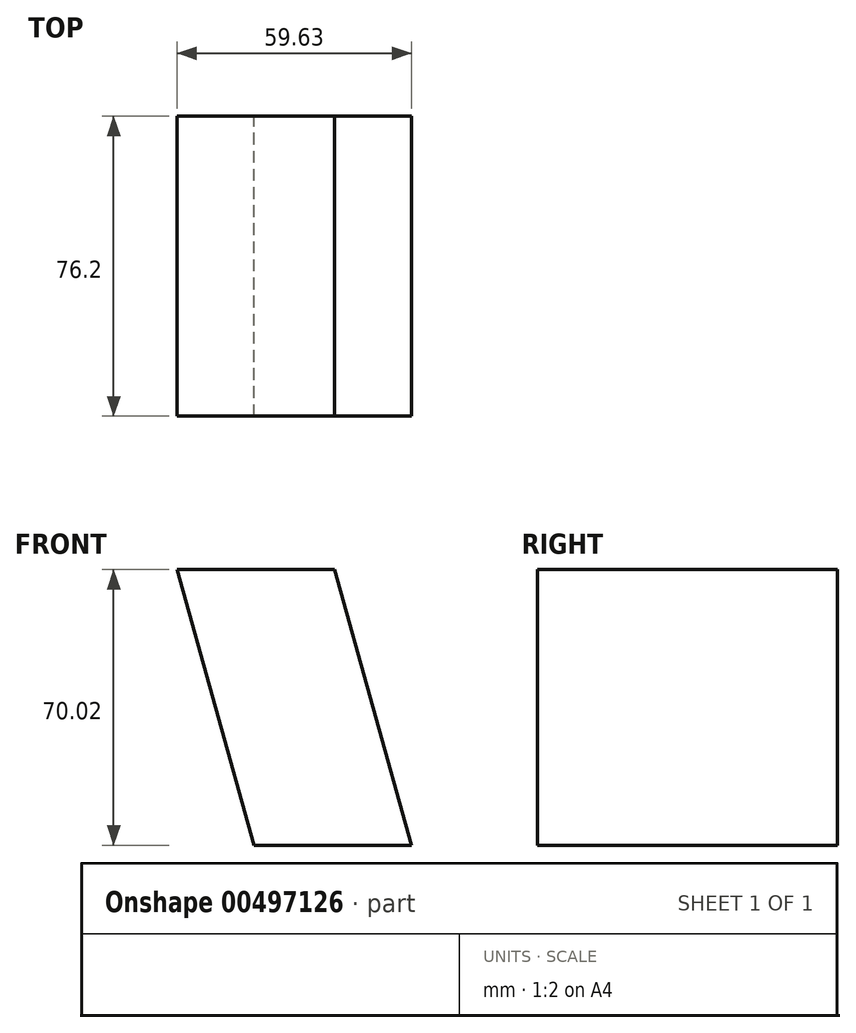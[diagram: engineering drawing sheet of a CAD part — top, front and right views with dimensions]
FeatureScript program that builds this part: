
annotation { "Feature Type Name" : "Feature", "Feature Type Description" : "" }
export const myFeature = defineFeature(function(context is Context, id is Id, definition is map)
    precondition{}
    {
        {
            var Q0;
            Q0=qCreatedBy(makeId("Front.planeOp"),FACE);
            var sketch = newSketch(context, id + "F0", { "sketchPlane" : qUnion([Q0])});
            skLineSegment(sketch, "E0", {"start": v(-65.28, 39.27) * mm, "end": v(-25.27, 39.27) * mm});
            skLineSegment(sketch, "E1", {"start": v(-25.27, 39.27) * mm, "end": v(-5.65, -30.75) * mm});
            skLineSegment(sketch, "E2", {"start": v(-5.65, -30.75) * mm, "end": v(-45.65, -30.75) * mm});
            skLineSegment(sketch, "E3", {"start": v(-45.65, -30.75) * mm, "end": v(-65.28, 39.27) * mm});
            skSolve(sketch);
        }
        {
            var Q0;
            Q0=makeQuery(id+"F0.imprint","IMPRINT",FACE,{"disambiguationData":[TD([[makeQuery(id+"F0.imprint","IMPRINT",EDGE,{"derivedFrom":sQuery(id+"F0.wireOp",EDGE,"E0")}),-1.0]])]});
            extrude(context, id + "F1", {"entities" : qUnion([Q0]), "depth" : 76.2 * mm});
        }
    });
